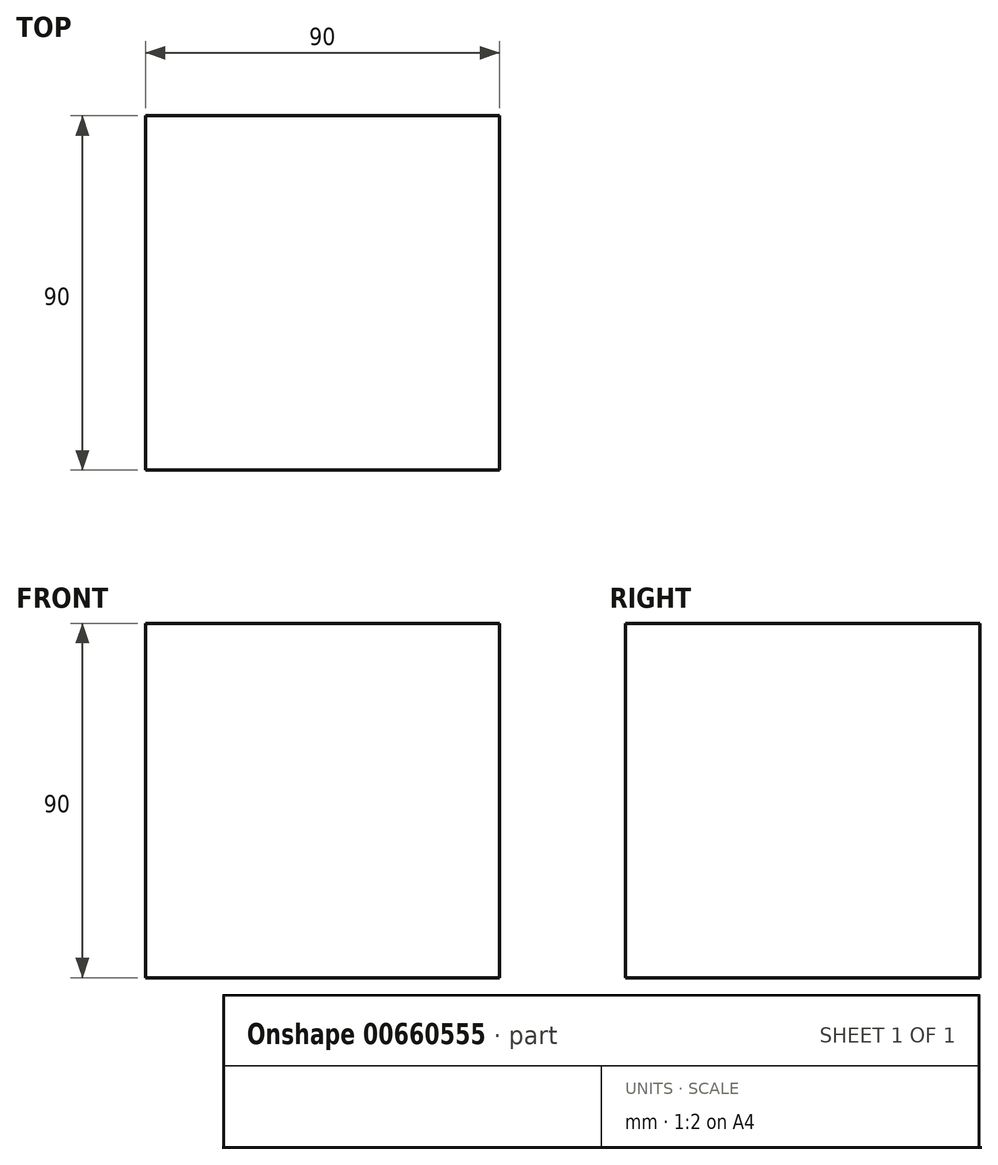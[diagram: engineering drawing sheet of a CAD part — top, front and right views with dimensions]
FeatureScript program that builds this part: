
annotation { "Feature Type Name" : "Feature", "Feature Type Description" : "" }
export const myFeature = defineFeature(function(context is Context, id is Id, definition is map)
    precondition{}
    {
        {
            var Q0;
            Q0=qCreatedBy(makeId("Top.planeOp"),FACE);
            var sketch = newSketch(context, id + "F0", { "sketchPlane" : qUnion([Q0])});
            skLineSegment(sketch, "E0.bottom", {"start": v(45, 45) * mm, "end": v(-45, 45) * mm});
            skLineSegment(sketch, "E0.top", {"start": v(45, -45) * mm, "end": v(-45, -45) * mm});
            skLineSegment(sketch, "E0.left", {"start": v(45, 45) * mm, "end": v(45, -45) * mm});
            skLineSegment(sketch, "E0.right", {"start": v(-45, 45) * mm, "end": v(-45, -45) * mm});
            skPoint(sketch, "E0.middle", {"position": v(0, 0) * mm});
            skSolve(sketch);
        }
        {
            var Q0;
            Q0 = qSketchRegion(id + "F0", true);
            extrude(context, id + "F1", {"entities" : qUnion([Q0]), "depth" : 90 * mm, "offsetDistance" : 25 * mm});
        }
    });
